# Revit family: KNS_LM_LS_Разветвитель Т-образный плавный LESTA_IEK
name_source: partatom
category: Соединительные детали кабельных лотков
units: mm (PartAtom-declared; Revit-internal decimal feet)

## family parameters
Всегда вертикально = Да
Заголовок OmniClass = Cable Trays and Horizontal Racks
На основе рабочей плоскости = Нет
Номер OmniClass = 23.80.30.17.17
Общий = Нет
При загрузке вырезать с полостями = Нет
Размер круглого соединителя = Использовать диаметр
Тип детали = Тройник ступенчатого

## types (4) — shared parameters
ADSK_Версия Revit = 2019
ADSK_Версия семейства = 1.2
ADSK_Группирование = Кабельные лотки и аксессуары
ADSK_Единица измерения = шт
ADSK_Завод-изготовитель = IEK
ADSK_Марка = LESTA
ADSK_Материал = <По категории>
ADSK_Материал обозначение = Сталь
ETIM_Class version = 7
IEK_Гарантийный срок = 3 года
IEK_Срок службы = 20 лет
URL = https://www.iek.ru
Изготовитель = IEK

## per-type parameters (varying)
| type | ADSK_Наименование краткое | IEK_Описание | IEK_Поиск в таблице имен | Радиус | Тип крышки |
| OS_R300 | Разветвитель лестничный LESTA Т-образный R300 OS IEK | Применяется для организации Т-образного ответвления кабельной трассы. Крышка поставляется отдельно.
Отсутствие острых кромок благодаря применению специальной технологии скругления до безопасного радиуса 5мм.
Надежное соединение перемычек к лонжерону - двойная заклепка.
Усиленная конструкция Т/Х - отводов. Благодаря применению пластины в основании толщиной 1мм.
Выштамповка на лонжероне позволяет устанавливать крышку без применения специальных аксессуаров. | KNS_LM_LS_Разветвитель Т-образный | 300 мм | KNS_LM_LS_Крышка разветвителя Т-обр плавного LESTA_IEK : OS_R300 |
| HDZ_R300 | Разветвитель лестничный LESTA Т-образный R300 HDZ IEK |  | KNS_LM_LS_Разветвитель Т-образный_HDZ | 300 мм | KNS_LM_LS_Крышка разветвителя Т-обр плавного LESTA_IEK : HDZ_R300 |
| OS_R600 | Разветвитель лестничный LESTA Т-образный R600 OS IEK | Применяется для организации Т-образного ответвления кабельной трассы. Крышка поставляется отдельно.
Отсутствие острых кромок благодаря применению специальной технологии скругления до безопасного радиуса 5мм.
Надежное соединение перемычек к лонжерону - двойная заклепка.
Усиленная конструкция Т/Х - отводов. Благодаря применению пластины в основании толщиной 1мм.
Выштамповка на лонжероне позволяет устанавливать крышку без применения специальных аксессуаров. | KNS_LM_LS_Разветвитель Т-образный | 600 мм | KNS_LM_LS_Крышка разветвителя Т-обр плавного LESTA_IEK : OS_R600 |
| HDZ_R600 | Разветвитель лестничный LESTA Т-образный R600 HDZ IEK |  | KNS_LM_LS_Разветвитель Т-образный_HDZ | 600 мм | KNS_LM_LS_Крышка разветвителя Т-обр плавного LESTA_IEK : HDZ_R600 |
